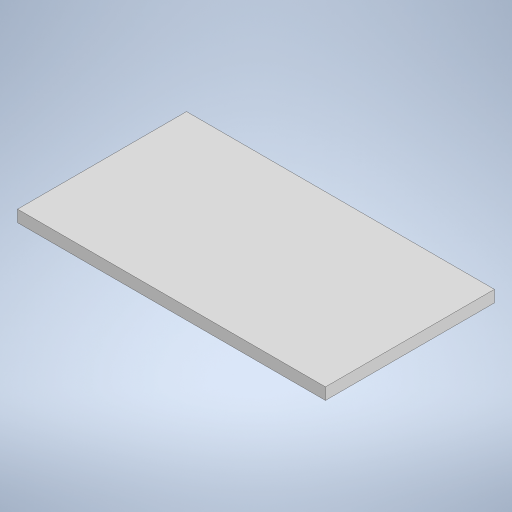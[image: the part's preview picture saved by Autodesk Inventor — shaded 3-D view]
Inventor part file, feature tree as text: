
AUTODESK INVENTOR PART (.ipt)
format: ipt  version: 2024 (Build 280153000, 153)  size: 204,800 bytes
history: native  units: mm
features: extrude x1, sketch x1
ambient origin geometry x8: Origin, YZ Plane, XZ Plane, XY Plane, X Axis, Y Axis, Z Axis, Center Point
bodies: Solid1 (feature_tree)
feature tree (2):
  extrude  "Extrusion1"  Depth=45.0mm
  sketch  "Sketch1"  dims[d0=82.0mm d1=45.0mm d2=3.125mm d3=0.0mm]
